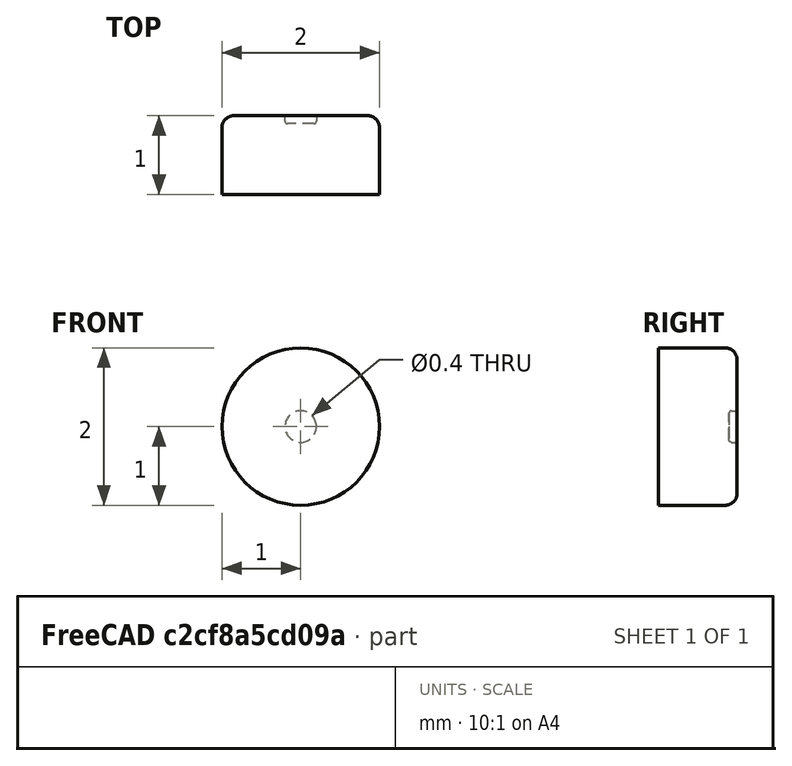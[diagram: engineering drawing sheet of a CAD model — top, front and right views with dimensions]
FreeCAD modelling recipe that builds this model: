
FCSTD DOCUMENT  (FreeCAD 0.16R6712 (Git))
Label: fixtop
License: All rights reserved
LicenseURL: http://en.wikipedia.org/wiki/All_rights_reserved
objects: Sketcher::SketchObject×2, PartDesign::Fillet×2, PartDesign::Pad×1, PartDesign::Pocket×1, Mesh::Feature×1
note: 8 computed .brp shape members not serialized (recipe doc carries the construction recipe); baked Part::Feature solids carry a one-line shape summary decoded from their .brp

FEATURE [Sketcher::SketchObject] Sketch
  Placement = pos=(0,0,0) rot=(1,0,0;1.5708rad)
  sketch-geometry (1):
    g0: Circle CenterX=0 CenterY=0 CenterZ=0 NormalX=0 NormalY=0 NormalZ=1 Radius=1
  constraints (1):
    c: Radius(g0) = 1
FEATURE [PartDesign::Pad] Pad
  Length = 1
  Length2 = 100
  Placement = pos=(0,0,0) rot=(1,0,0;1.5708rad)
  Reversed = true
  Sketch = -> Sketch
  Type = 0
FEATURE [PartDesign::Fillet] Fillet
  Base = -> Pad [Edge3]
  Placement = pos=(0,0,0) rot=(1,0,0;1.5708rad)
  Radius = 0.15
FEATURE [Sketcher::SketchObject] Sketch001
  Placement = pos=(0,1,0) rot=(-1,0,0;1.5708rad)
  Support = -> Fillet [Face4]
  sketch-geometry (1):
    g0: Circle CenterX=0 CenterY=0 CenterZ=0 NormalX=0 NormalY=0 NormalZ=1 Radius=0.2
  constraints (2):
    c: Coincident(g0,g-1)
    c: Radius(g0) = 0.2
FEATURE [PartDesign::Pocket] Pocket
  Length = 0.1
  Placement = pos=(0,0,0) rot=(1,0,0;1.5708rad)
  Sketch = -> Sketch001
  Type = 0
FEATURE [PartDesign::Fillet] Fillet001
  Base = -> Pocket [Edge6,Edge8]
  Placement = pos=(0,0,0) rot=(1,0,0;1.5708rad)
  Radius = 0.03
FEATURE [Mesh::Feature] Mesh001  label="Fillet001 (Meshed)"
  Placement = pos=(0,-3.7,0) rot=(0,0,1;0rad)
